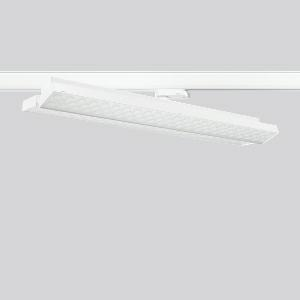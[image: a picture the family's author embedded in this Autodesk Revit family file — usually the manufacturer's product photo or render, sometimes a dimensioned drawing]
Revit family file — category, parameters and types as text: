
# Revit family: tx-move_742162_002_1_76_c556
name_source: partatom
category: Lighting Fixtures
units: mm (PartAtom-declared; Revit-internal decimal feet)

## family parameters
Cut with Voids When Loaded = No
Host = Face
Light Source = No
Part Type = Normal
Room Calculation Point = No
Round Connector Dimension = Use Diameter
Shared = No

## types (1)
- MultiLumen 1 (1 x LED Modul 840, 3150 lm, 4000)
    Apparent Load = 41 VA
    CIE Flux Codes = 77 96 99 100 100
    Color Rendering = 80
    Color Temperature = 4000
    Default Elevation = 1800 mm
    Description = Series: TX-MOVE
Multifunctional surface-mounted spotlight for area lighting. Very flat design. Housing: sheet steel, powder-coated. Rotation range: 356°. Swivel range: 90°. Consistent alignment possible with visible tilt scale. High-efficiency LED units with optimum light control thanks to clear plastic (PC) lens optics. Spezielle Mikrostrukturen reduzieren Gelbsaum. Symmetrical light distribution. With adapter for RZB 3-circuit DALI tracks. Suitable for Track on ceiling. MultiLumen: Luminous flux adjustable in 3 steps. Factory setting is the highest luminous flux. Environmentally friendly and resource-saving due to replaceable and recyclable components. 
Colour: traffic white, matt (RAL 9016)
Length: 570 mm
Width: 119 mm
Height: 88 mm
Lamp: LED
Socket: without socket
Colour temperature: 4000K
Colour rendering index (CRI): 80
System power: 41 W
Rated luminous flux: 6300 lm
Luminous efficiency: 154 lm/W
System power 2: 57 W
Rated luminous flux 2: 8550 lm
Luminous efficiency 2: 150 lm/W
System power 3: 73 W
Rated luminous flux 3: 10400 lm
Luminous efficiency 3: 142 lm/W
Control gear: Dimmable EVG, DALI
Protection class: I
Type of protection: IP 20
    Height = 75 mm
    Lamp = 1 x LED Modul 840
    Lamp Light Flux = 3150 lm
    Lamp count = 1
    Length = 569 mm
    Lifetime = 50000 h
    Luminous efficacy = 154 lm/W
    Manufacturer = RZB
    ModVariant = No
    Model = 742162.002.1.76
    Mounting Place = Ceiling
    Mounting Type = Surface mounted
    Number of Poles = 1
    OnlyDefault = Yes
    Power Factor = 1
    Product Name = TX-MOVE
    Product group = Track mounted projectors
    ProductGroupID = 301
    Protection Class = Protection class I
    Protection Degree = IP 20
    RLX_Detail_Level = 1
    RLX_Emergency_Light_Flux = 0 lm
    RLX_Emergency_Type = 0
    RLX_Emergency_Type_DB = No
    RlxData = <blob elided: 31209 chars, md5=18d4f140>
    Socket = socket
    Standby Power = 0 W
    System Light Flux = 6300 lm
    System Power = 41 W
    Type Comments = MultiLumen 1
    Type Image = 742162.002.jpg
    URL = http://relux.com
    VarID = multilumen_1
    Voltage = 0 V
    Weight = 0.00 kg
    Width = 119 mm

## geometry (parser evidence)
native form markers: Blend x4, Sweep x14
no freeform markers — native parametric forms only
